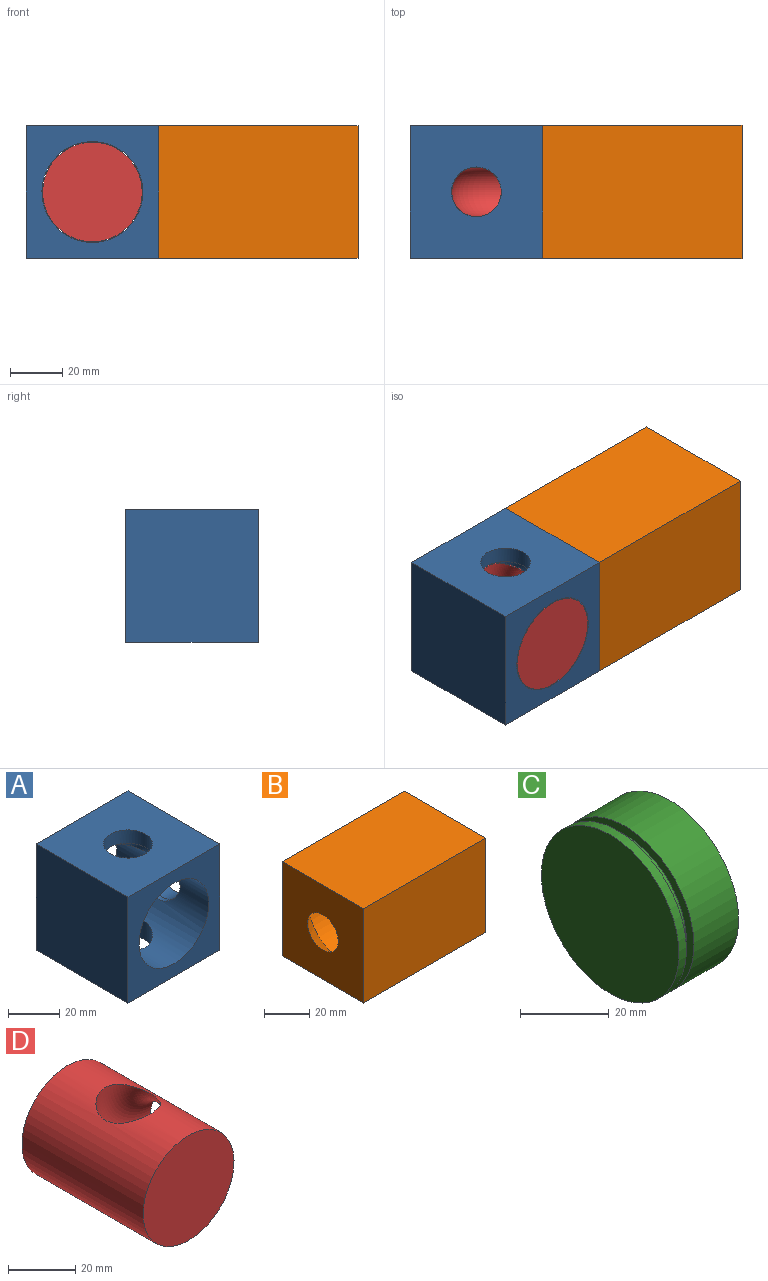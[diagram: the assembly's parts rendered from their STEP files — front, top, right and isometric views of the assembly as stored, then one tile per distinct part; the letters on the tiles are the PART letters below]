
ASSEMBLY  parts=4 mates=3
PART A: 14 faces, bbox 50.8x50.8x50.8 mm
  f0: plane 50.8x50.8mm, normal (1,0,0), area 2295.6mm2, adj f1,f3,f5,f6,f10
  f1: plane 50.8x50.8mm, normal (0,0,1), area 2295.6mm2, adj f0,f2,f5,f6,f7
  f2: plane 50.8x50.8mm, normal (-1,0,0), area 2580.6mm2, adj f1,f3,f5,f6
  f3: plane 50.8x50.8mm, normal (0,0,-1), area 2295.6mm2, adj f0,f2,f5,f6,f13
  f4: cylinder r=19.3mm len=50.8mm, axis (0,-1,0), area 5273.5mm2, adj f5,f6,f7,f8,f9,f10,f11,f12
  f5: plane 50.8x50.8mm, normal (0,1,0), area 1409.9mm2, adj f0,f1,f2,f3,f4
  f6: plane 50.8x50.8mm, normal (0,-1,0), area 1409.9mm2, adj f0,f1,f2,f3,f4
  f7: cylinder r=9.53mm len=19.05mm, axis (0,0,1), area 377.9mm2, adj f1,f4,f8,f9
  f8: torus R=19.05mm, axis (0,1,0), area 32.2mm2, adj f4,f7
  f9: torus R=19.05mm, axis (0,1,0), area 30mm2, adj f4,f7
  f10: cylinder r=9.53mm len=19.05mm, axis (-1,0,0), area 377.9mm2, adj f0,f4,f11,f12
  f11: torus R=19.05mm, axis (0,1,0), area 32.2mm2, adj f4,f10
  f12: torus R=19.05mm, axis (0,1,0), area 30mm2, adj f4,f10
  f13: cylinder r=9.53mm len=19.05mm, axis (0,0,-1), area 438.7mm2, adj f3,f4
PART B: 8 faces, bbox 76.2x50.8x50.8 mm
  f0: plane 76.2x50.8mm, normal (0,-1,0), area 3871mm2, adj f1,f2,f3,f4
  f1: plane 50.8x50.8mm, normal (-1,0,0), area 2295.6mm2, adj f0,f2,f3,f5,f7
  f2: plane 76.2x50.8mm, normal (0,0,1), area 3871mm2, adj f0,f1,f4,f5
  f3: plane 76.2x50.8mm, normal (0,0,-1), area 3871mm2, adj f0,f1,f4,f5
  f4: plane 50.8x50.8mm, normal (1,0,0), area 1028.8mm2, adj f0,f2,f3,f5,f6
  f5: plane 76.2x50.8mm, normal (0,1,0), area 3871mm2, adj f1,f2,f3,f4
  f6: cylinder r=22.23mm len=63.5mm, axis (1,0,0), area 8867.4mm2, adj f4,f7
  f7: cone r=9.53mm half-angle=45deg, axis (1,0,0), area 1791.5mm2, adj f1,f6
PART C: 11 faces, bbox 19.1x43.9x43.9 mm
  f0: cylinder r=21.97mm len=43.94mm, axis (1,0,0), area 1972.4mm2, adj f1,f6
  f1: plane 43.94x43.94mm, normal (-1,0,0), area 310.9mm2, adj f0,f2
  f2: cylinder r=19.59mm len=39.18mm, axis (1,0,0), area 293.1mm2, adj f1,f3
  f3: plane 43.94x43.94mm, normal (1,0,0), area 310.9mm2, adj f2,f4
  f4: cylinder r=21.97mm len=43.94mm, axis (1,0,0), area 328.7mm2, adj f3,f5
  f5: plane 43.94x43.94mm, normal (-1,0,0), area 1516.5mm2, adj f4
  f6: plane 43.94x43.94mm, normal (1,0,0), area 330.4mm2, adj f0,f8
  f7: plane 34.1x34.1mm, normal (1,0,0), area 913.2mm2, adj f10
  f8: cylinder r=19.43mm len=38.86mm, axis (1,0,0), area 1434.2mm2, adj f6,f9
  f9: plane 38.86x38.86mm, normal (1,0,0), area 272.9mm2, adj f8,f10
  f10: cylinder r=17.05mm len=34.1mm, axis (1,0,0), area 510.2mm2, adj f7,f9
PART D: 4 faces, bbox 38.1x50.8x38.1 mm
  f0: cylinder r=19.05mm len=50.8mm, axis (0,-1,0), area 5484.8mm2, adj f1,f2,f3
  f1: plane 38.1x38.1mm, normal (0,1,0), area 1140.1mm2, adj f0
  f2: plane 38.1x38.1mm, normal (0,-1,0), area 1140.1mm2, adj f0
  f3: torus R=19.05mm, axis (0,1,0), area 1636.9mm2, adj f0
PLACE A at identity fixed
PLACE B at identity
PLACE C t=(-6.35,0,0)mm
PLACE D at identity
MATE slider C.f0 <-> B.f6  axis (1,0,0) through (95.25,0,0)mm
MATE revolute D.f0 <-> A.f4  axis (0,-1,0) through (0,-25.4,0)mm
MATE fastened B.f1 <-> A.f0  axis (-1,0,0) through (25.4,-25.4,25.4)mm
